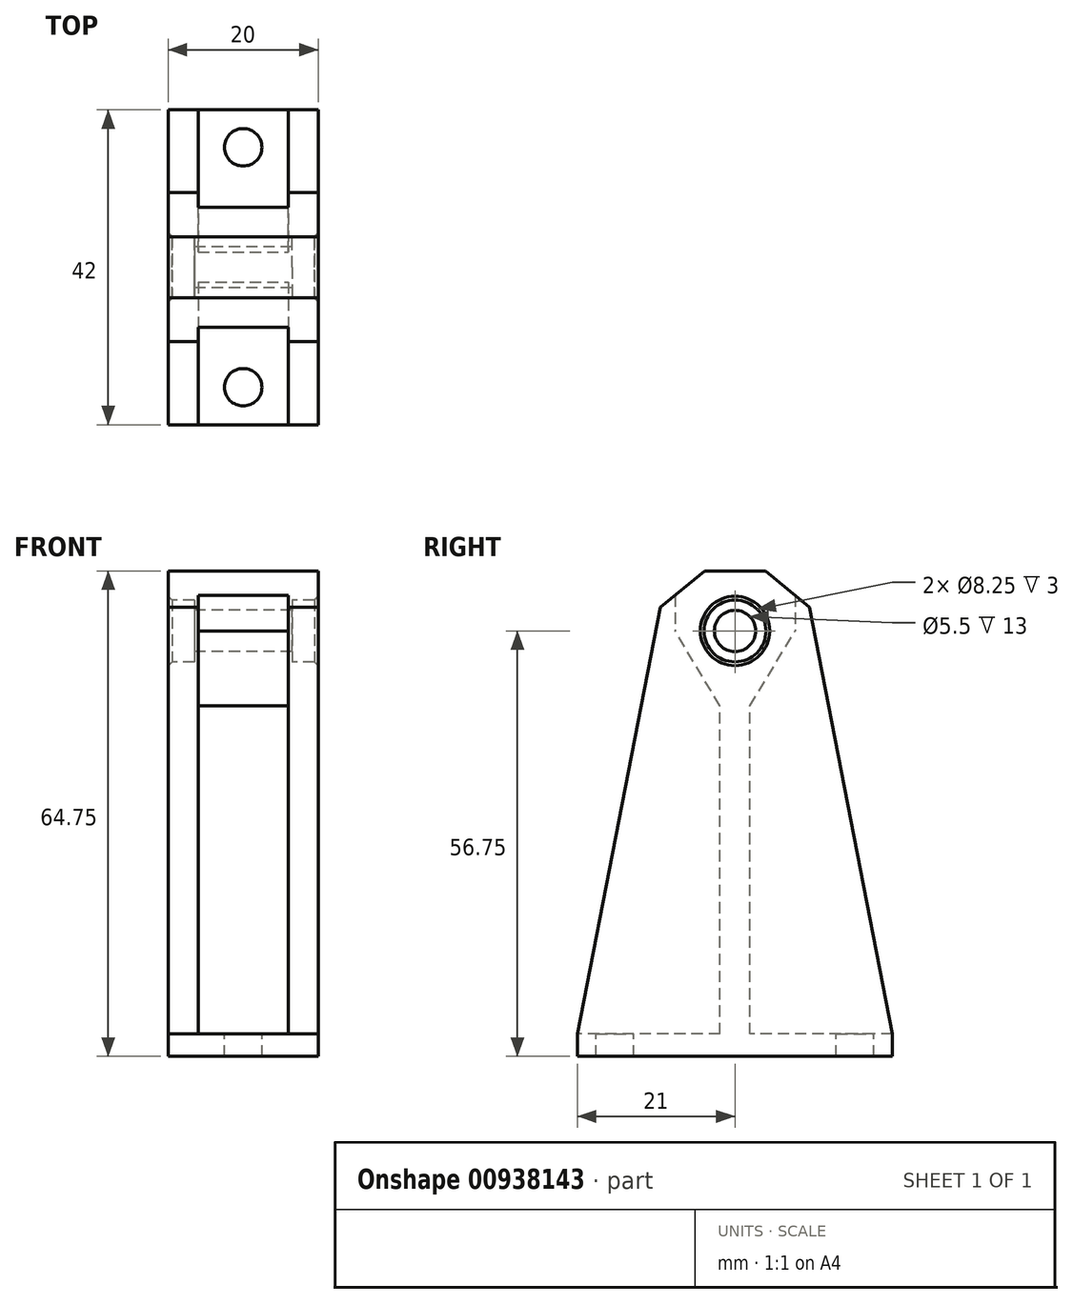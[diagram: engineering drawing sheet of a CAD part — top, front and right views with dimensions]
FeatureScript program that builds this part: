
annotation { "Feature Type Name" : "Feature", "Feature Type Description" : "" }
export const myFeature = defineFeature(function(context is Context, id is Id, definition is map)
    precondition{}
    {
        {
            var Q0;
            Q0=qCreatedBy(makeId("Top.planeOp"),FACE);
            var sketch = newSketch(context, id + "F0", { "sketchPlane" : qUnion([Q0])});
            skCircle(sketch, "E0", {"center": v(0, 16) * mm, "radius": 2.5 * mm});
            skCircle(sketch, "E1", {"center": v(0, -16) * mm, "radius": 2.5 * mm});
            skLineSegment(sketch, "E2.bottom", {"start": v(10, 21) * mm, "end": v(-10, 21) * mm});
            skLineSegment(sketch, "E2.top", {"start": v(10, -21) * mm, "end": v(-10, -21) * mm});
            skLineSegment(sketch, "E2.left", {"start": v(10, 21) * mm, "end": v(10, -21) * mm});
            skLineSegment(sketch, "E2.right", {"start": v(-10, 21) * mm, "end": v(-10, -21) * mm});
            skLineSegment(sketch, "E3", {"start": v(-6, 21) * mm, "end": v(-6, -21) * mm});
            skLineSegment(sketch, "E4", {"start": v(6, 21) * mm, "end": v(6, -21) * mm});
            skLineSegment(sketch, "E5.bottom", {"start": v(-6, -2) * mm, "end": v(6, -2) * mm});
            skLineSegment(sketch, "E5.top", {"start": v(-6, 2) * mm, "end": v(6, 2) * mm});
            skLineSegment(sketch, "E5.left", {"start": v(-6, -2) * mm, "end": v(-6, 2) * mm});
            skLineSegment(sketch, "E5.right", {"start": v(6, -2) * mm, "end": v(6, 2) * mm});
            skPoint(sketch, "E5.middle", {"position": v(0, 0) * mm});
            skPoint(sketch, "E6", {"position": v(-10, 0) * mm});
            skSolve(sketch);
        }
        {
            var Q0;
            Q0=makeQuery(id+"F0.imprint","IMPRINT",FACE,{"disambiguationData":[TD([[makeQuery(id+"F0.imprint","IMPRINT",EDGE,{"derivedFrom":sQuery(id+"F0.wireOp",EDGE,"E0")}),-1.0]])]});
            var Q1;
            {var subQ4=sQuery(id+"F0.wireOp",EDGE,"E2.left");Q1=makeQuery(id+"F0.imprint","IMPRINT",FACE,{"disambiguationData":[TD([[makeQuery(id+"F0.imprint","IMPRINT",EDGE,{"derivedFrom":subQ4}),-1.0]])]});}
            var Q2;
            Q2=makeQuery(id+"F0.imprint","IMPRINT",FACE,{"disambiguationData":[TD([[makeQuery(id+"F0.imprint","IMPRINT",EDGE,{"derivedFrom":sQuery(id+"F0.wireOp",EDGE,"E1")}),-1.0]])]});
            var Q3;
            {var subQ4=sQuery(id+"F0.wireOp",EDGE,"E2.right");Q3=makeQuery(id+"F0.imprint","IMPRINT",FACE,{"disambiguationData":[TD([[makeQuery(id+"F0.imprint","IMPRINT",EDGE,{"derivedFrom":subQ4}),1.0]])]});}
            var Q4;
            {var subQ0=sQuery(id+"F0.wireOp",EDGE,"jyKhno33-epqN-gYMh-0gIM-PIKnwXsBvOFv");Q4=makeQuery(id+"F0.imprint","IMPRINT",FACE,{"disambiguationData":[TD([[makeQuery(id+"F0.imprint","IMPRINT",EDGE,{"derivedFrom":subQ0}),-1.0]])]});}
            var Q5;
            {var subQ0=sQuery(id+"F0.wireOp",EDGE,"E5.bottom");Q5=makeQuery(id+"F0.imprint","IMPRINT",FACE,{"disambiguationData":[TD([[makeQuery(id+"F0.imprint","IMPRINT",EDGE,{"derivedFrom":subQ0}),1.0]])]});}
            extrude(context, id + "F1", {"entities" : qUnion([Q0, Q1, Q2, Q3, Q4, Q5]), "oppositeDirection" : true, "depth" : 3 * mm, "offsetDistance" : 25 * mm});
        }
        {
            var Q0;
            Q0=qCreatedBy(makeId("Right.planeOp"),FACE);
            var sketch = newSketch(context, id + "F2", { "sketchPlane" : qUnion([Q0])});
            skLineSegment(sketch, "E7", {"start": v(-8.77, 43.75) * mm, "end": v(8.77, 43.75) * mm, "construction": true});
            skPoint(sketch, "E8", {"position": v(0, 43.75) * mm});
            skLineSegment(sketch, "E9", {"start": v(8.77, 53.75) * mm, "end": v(-8.77, 53.75) * mm, "construction": true});
            skLineSegment(sketch, "E10", {"start": v(-8.77, 61.75) * mm, "end": v(8.77, 61.75) * mm, "construction": true});
            skSolve(sketch);
        }
        {
            var Q0;
            Q0=sQuery(id+"F2.wireOp",EDGE,"E7");
            cPlane(context, id + "F3", {"entities" : qUnion([Q0]), "cplaneType" : CPlaneType.LINE_ANGLE, "offset" : 25 * mm, "angle" : 0 * degree, "width" : 150 * mm, "height" : 150 * mm});
        }
        {
            var Q0;
            Q0=qCreatedBy(id+"F3.planeOp",FACE);
            var sketch = newSketch(context, id + "F4", { "sketchPlane" : qUnion([Q0])});
            skLineSegment(sketch, "E11.bottom", {"start": v(6, 2) * mm, "end": v(-6, 2) * mm});
            skLineSegment(sketch, "E11.top", {"start": v(6, -2) * mm, "end": v(-6, -2) * mm});
            skLineSegment(sketch, "E11.left", {"start": v(6, 2) * mm, "end": v(6, -2) * mm});
            skLineSegment(sketch, "E11.right", {"start": v(-6, 2) * mm, "end": v(-6, -2) * mm});
            skPoint(sketch, "E11.middle", {"position": v(0, 0) * mm});
            skSolve(sketch);
        }
        {
            var Q0;
            Q0=sQuery(id+"F2.wireOp",EDGE,"E9");
            cPlane(context, id + "F5", {"entities" : qUnion([Q0]), "cplaneType" : CPlaneType.LINE_ANGLE, "offset" : 25 * mm, "angle" : 0 * degree, "width" : 150 * mm, "height" : 150 * mm});
        }
        {
            var Q0;
            Q0=qCreatedBy(id+"F5.planeOp",FACE);
            var sketch = newSketch(context, id + "F6", { "sketchPlane" : qUnion([Q0])});
            skLineSegment(sketch, "E12.bottom", {"start": v(6, -8) * mm, "end": v(-6, -8) * mm});
            skLineSegment(sketch, "E12.top", {"start": v(6, 8) * mm, "end": v(-6, 8) * mm});
            skLineSegment(sketch, "E12.left", {"start": v(6, -8) * mm, "end": v(6, 8) * mm});
            skLineSegment(sketch, "E12.right", {"start": v(-6, -8) * mm, "end": v(-6, 8) * mm});
            skPoint(sketch, "E12.middle", {"position": v(0, 0) * mm});
            skSolve(sketch);
        }
        {
            var Q0;
            Q0=sQuery(id+"F2.wireOp",EDGE,"E10");
            cPlane(context, id + "F7", {"entities" : qUnion([Q0]), "cplaneType" : CPlaneType.LINE_ANGLE, "offset" : 25 * mm, "angle" : 0 * degree, "width" : 150 * mm, "height" : 150 * mm});
        }
        {
            var Q0;
            Q0=qCreatedBy(id+"F7.planeOp",FACE);
            var sketch = newSketch(context, id + "F8", { "sketchPlane" : qUnion([Q0])});
            skLineSegment(sketch, "E13.bottom", {"start": v(-6, 9) * mm, "end": v(-10, 9) * mm});
            skLineSegment(sketch, "E13.top", {"start": v(-6, -9) * mm, "end": v(-10, -9) * mm});
            skLineSegment(sketch, "E13.left", {"start": v(-6, 9) * mm, "end": v(-6, -9) * mm});
            skLineSegment(sketch, "E13.right", {"start": v(-10, 9) * mm, "end": v(-10, -9) * mm});
            skPoint(sketch, "E13.middle", {"position": v(-8, 0) * mm});
            skLineSegment(sketch, "E14.bottom", {"start": v(10, 9) * mm, "end": v(6, 9) * mm});
            skLineSegment(sketch, "E14.top", {"start": v(10, -9) * mm, "end": v(6, -9) * mm});
            skLineSegment(sketch, "E14.left", {"start": v(10, 9) * mm, "end": v(10, -9) * mm});
            skLineSegment(sketch, "E14.right", {"start": v(6, 9) * mm, "end": v(6, -9) * mm});
            skPoint(sketch, "E14.middle", {"position": v(8, 0) * mm});
            skLineSegment(sketch, "E15", {"start": v(-8, 0) * mm, "end": v(8, 0) * mm, "construction": true});
            skPoint(sketch, "E16.middle", {"position": v(0, 0) * mm});
            skSolve(sketch);
        }
        {
            var Q0;
            {var subQ0=sQuery(id+"F0.wireOp",EDGE,"E5.bottom");Q0=makeQuery(id+"F0.imprint","IMPRINT",FACE,{"disambiguationData":[TD([[makeQuery(id+"F0.imprint","IMPRINT",EDGE,{"derivedFrom":subQ0}),1.0]])]});}
            var Q1;
            Q1=makeQuery(id+"F4.imprint","IMPRINT",FACE,{"disambiguationData":[TD([[makeQuery(id+"F4.imprint","IMPRINT",EDGE,{"derivedFrom":sQuery(id+"F4.wireOp",EDGE,"E11.bottom")}),1.0]])]});
            loft(context, id + "F9", {"operationType" : NewBodyOperationType.ADD, "sheetProfilesArray" : [{ "sheetProfileEntities" : qUnion([Q0]) }, { "sheetProfileEntities" : qUnion([Q1]) }]});
        }
        {
            var Q0;
            Q0=makeQuery(id+"F4.imprint","IMPRINT",FACE,{"disambiguationData":[TD([[makeQuery(id+"F4.imprint","IMPRINT",EDGE,{"derivedFrom":sQuery(id+"F4.wireOp",EDGE,"E11.bottom")}),1.0]])]});
            var Q1;
            Q1=makeQuery(id+"F6.imprint","IMPRINT",FACE,{"disambiguationData":[TD([[makeQuery(id+"F6.imprint","IMPRINT",EDGE,{"derivedFrom":sQuery(id+"F6.wireOp",EDGE,"E12.bottom")}),-1.0]])]});
            loft(context, id + "F10", {"operationType" : NewBodyOperationType.ADD, "sheetProfilesArray" : [{ "sheetProfileEntities" : qUnion([Q0]) }, { "sheetProfileEntities" : qUnion([Q1]) }]});
        }
        {
            var Q0;
            {var subQ4=sQuery(id+"F0.wireOp",EDGE,"E2.left");Q0=makeQuery(id+"F0.imprint","IMPRINT",FACE,{"disambiguationData":[TD([[makeQuery(id+"F0.imprint","IMPRINT",EDGE,{"derivedFrom":subQ4}),-1.0]])]});}
            var Q1;
            {var subQ4=sQuery(id+"F8.wireOp",EDGE,"E14.bottom");Q1=makeQuery(id+"F8.imprint","IMPRINT",FACE,{"disambiguationData":[TD([[makeQuery(id+"F8.imprint","IMPRINT",EDGE,{"derivedFrom":subQ4}),1.0]])]});}
            loft(context, id + "F11", {"operationType" : NewBodyOperationType.ADD, "sheetProfilesArray" : [{ "sheetProfileEntities" : qUnion([Q0]) }, { "sheetProfileEntities" : qUnion([Q1]) }]});
        }
        {
            var Q0;
            Q0=makeQuery(id+"F8.imprint","IMPRINT",FACE,{"disambiguationData":[TD([[makeQuery(id+"F8.imprint","IMPRINT",EDGE,{"derivedFrom":sQuery(id+"F8.wireOp",EDGE,"E13.bottom")}),1.0]])]});
            var Q1;
            {var subQ4=sQuery(id+"F0.wireOp",EDGE,"E2.right");Q1=makeQuery(id+"F0.imprint","IMPRINT",FACE,{"disambiguationData":[TD([[makeQuery(id+"F0.imprint","IMPRINT",EDGE,{"derivedFrom":subQ4}),1.0]])]});}
            var Q2;
            Q2=makeQuery(id+"F9.opLoft","SWEPT_EDGE",EDGE,{"disambiguationData":[OSD([sQuery(id+"F0.wireOp",EDGE,"jyKhno33-epqN-gYMh-0gIM-PIKnwXsBvOFv"),sQuery(id+"F0.wireOp",EDGE,"E3"),sQuery(id+"F4.wireOp",EDGE,"E11.bottom"),sQuery(id+"F4.wireOp",EDGE,"E11.right")])]});
            var Q4;
            Q4=sQuery(id+"F0.wireOp",VERTEX,"E3.start");
            var Q5;
            Q5=sQuery(id+"F8.wireOp",VERTEX,"E13.bottom.start");
            loft(context, id + "F12", {"operationType" : NewBodyOperationType.ADD, "sheetProfilesArray" : [{ "sheetProfileEntities" : qUnion([Q0]) }, { "sheetProfileEntities" : qUnion([Q1]) }], "guidesArray" : [{ "guideEntities" : qUnion([Q2]), "guideDerivativeType" : LoftGuideDerivativeType.DEFAULT, "guideDerivativeMagnitude" : 1 }], "matchConnections" : true, "connections" : [{ "connectionEntities" : qUnion([Q4, Q5]), "connectionEdgeQueries" : qUnion([]), "connectionEdgeParameters" : [] }]});
        }
        {
            var Q0;
            Q0=makeQuery(id+"F6.imprint","IMPRINT",FACE,{"disambiguationData":[TD([[makeQuery(id+"F6.imprint","IMPRINT",EDGE,{"derivedFrom":sQuery(id+"F6.wireOp",EDGE,"E12.bottom")}),-1.0]])]});
            extrude(context, id + "F13", {"entities" : qUnion([Q0]), "operationType" : NewBodyOperationType.ADD, "oppositeDirection" : true, "depth" : 8 * mm, "offsetDistance" : 25 * mm});
        }
        {
            var Q0;
            Q0=makeQuery(id+"F11.opLoft","MID_CAP_EDGE",EDGE,{"disambiguationData":[OSD([sQuery(id+"F8.wireOp",EDGE,"E14.bottom"),sQuery(id+"F8.wireOp",EDGE,"E14.left"),sQuery(id+"F8.wireOp",EDGE,"E14.right")])],"capPos":1.0});
            var Q1;
            Q1=makeQuery(id+"F11.opLoft","MID_CAP_EDGE",EDGE,{"disambiguationData":[OSD([sQuery(id+"F8.wireOp",EDGE,"E14.top"),sQuery(id+"F8.wireOp",EDGE,"E14.left"),sQuery(id+"F8.wireOp",EDGE,"E14.right")])],"capPos":1.0});
            chamfer(context, id + "F14", {"entities" : qUnion([Q0, Q1]), "width" : 6 * mm, "tangentPropagation" : true});
        }
        {
            var Q0;
            {var subQ0=sQuery(id+"F0.wireOp",EDGE,"E2.right");Q0=makeQuery(id+"F12.boolean.opBoolean","MERGE",FACE,{"derivedFrom":[makeQuery(id+"F1.opExtrude","SWEPT_FACE",FACE,{"disambiguationData":[OSD([subQ0])]}),makeQuery(id+"F12.opLoft","SWEPT_FACE",FACE,{"disambiguationData":[OSD([sQuery(id+"F0.wireOp",EDGE,"E2.bottom"),sQuery(id+"F0.wireOp",EDGE,"E2.top"),subQ0,sQuery(id+"F8.wireOp",EDGE,"E13.bottom"),sQuery(id+"F8.wireOp",EDGE,"E13.top"),sQuery(id+"F8.wireOp",EDGE,"E13.right")])]})]});}
            var sketch = newSketch(context, id + "F15", { "sketchPlane" : qUnion([Q0])});
            skCircle(sketch, "E17", {"center": v(0, 53.75) * mm, "radius": 4.12 * mm});
            skCircle(sketch, "E18", {"center": v(0, 53.75) * mm, "radius": 2.75 * mm});
            skSolve(sketch);
        }
        {
            var Q0;
            {var subQ0=sQuery(id+"F0.wireOp",EDGE,"E2.left");Q0=makeQuery(id+"F11.boolean.opBoolean","MERGE",FACE,{"derivedFrom":[makeQuery(id+"F1.opExtrude","SWEPT_FACE",FACE,{"disambiguationData":[OSD([subQ0])]}),makeQuery(id+"F11.opLoft","SWEPT_FACE",FACE,{"disambiguationData":[OSD([sQuery(id+"F0.wireOp",EDGE,"E2.bottom"),sQuery(id+"F0.wireOp",EDGE,"E2.top"),subQ0,sQuery(id+"F8.wireOp",EDGE,"E14.bottom"),sQuery(id+"F8.wireOp",EDGE,"E14.top"),sQuery(id+"F8.wireOp",EDGE,"E14.left")])]})]});}
            var sketch = newSketch(context, id + "F16", { "sketchPlane" : qUnion([Q0])});
            skCircle(sketch, "E19", {"center": v(0, 53.75) * mm, "radius": 4.12 * mm});
            skSolve(sketch);
        }
        {
            var Q0;
            Q0=makeQuery(id+"F15.imprint","IMPRINT",FACE,{"disambiguationData":[TD([[makeQuery(id+"F15.imprint","IMPRINT",EDGE,{"derivedFrom":sQuery(id+"F15.wireOp",EDGE,"E18")}),1.0]])]});
            extrude(context, id + "F17", {"entities" : qUnion([Q0]), "operationType" : NewBodyOperationType.REMOVE, "endBound" : BoundingType.THROUGH_ALL, "oppositeDirection" : true, "depth" : 25 * mm, "offsetDistance" : 25 * mm});
        }
        {
            var Q0;
            Q0=makeQuery(id+"F15.imprint","IMPRINT",FACE,{"disambiguationData":[TD([[makeQuery(id+"F15.imprint","IMPRINT",EDGE,{"derivedFrom":sQuery(id+"F15.wireOp",EDGE,"E17")}),1.0]])]});
            var Q1;
            Q1=makeQuery(id+"F16.imprint","IMPRINT",FACE,{"disambiguationData":[TD([[makeQuery(id+"F16.imprint","IMPRINT",EDGE,{"derivedFrom":sQuery(id+"F16.wireOp",EDGE,"E19")}),1.0]])]});
            extrude(context, id + "F18", {"entities" : qUnion([Q0, Q1]), "operationType" : NewBodyOperationType.REMOVE, "endBound" : BoundingType.SYMMETRIC, "oppositeDirection" : true, "depth" : 7 * mm, "offsetDistance" : 25 * mm});
        }
        {
            var Q0;
            {var subQ0=sQuery(id+"F0.wireOp",EDGE,"E2.left");Q0=makeQuery(id+"F18.boolean.opBoolean","INTERSECT",EDGE,{"derivedFrom":[makeQuery(id+"F11.boolean.opBoolean","MERGE",FACE,{"derivedFrom":[makeQuery(id+"F1.opExtrude","SWEPT_FACE",FACE,{"disambiguationData":[OSD([subQ0])]}),makeQuery(id+"F11.opLoft","SWEPT_FACE",FACE,{"disambiguationData":[OSD([sQuery(id+"F0.wireOp",EDGE,"E2.bottom"),sQuery(id+"F0.wireOp",EDGE,"E2.top"),subQ0,sQuery(id+"F8.wireOp",EDGE,"E14.bottom"),sQuery(id+"F8.wireOp",EDGE,"E14.top"),sQuery(id+"F8.wireOp",EDGE,"E14.left")])]})]}),makeQuery(id+"F18.opExtrude","SWEPT_FACE",FACE,{"disambiguationData":[OSD([sQuery(id+"F16.wireOp",EDGE,"E19")])]})]});}
            var Q1;
            {var subQ0=sQuery(id+"F0.wireOp",EDGE,"E2.right");Q1=makeQuery(id+"F18.boolean.opBoolean","INTERSECT",EDGE,{"derivedFrom":[makeQuery(id+"F12.boolean.opBoolean","MERGE",FACE,{"derivedFrom":[makeQuery(id+"F1.opExtrude","SWEPT_FACE",FACE,{"disambiguationData":[OSD([subQ0])]}),makeQuery(id+"F12.opLoft","SWEPT_FACE",FACE,{"disambiguationData":[OSD([sQuery(id+"F0.wireOp",EDGE,"E2.bottom"),sQuery(id+"F0.wireOp",EDGE,"E2.top"),subQ0,sQuery(id+"F8.wireOp",EDGE,"E13.bottom"),sQuery(id+"F8.wireOp",EDGE,"E13.top"),sQuery(id+"F8.wireOp",EDGE,"E13.right")])]})]}),makeQuery(id+"F18.opExtrude","SWEPT_FACE",FACE,{"disambiguationData":[OSD([sQuery(id+"F15.wireOp",EDGE,"E17")])]})]});}
            chamfer(context, id + "F19", {"entities" : qUnion([Q0, Q1]), "width" : 0.5 * mm, "tangentPropagation" : true});
        }
    });
